FCSTD DOCUMENT  (FreeCAD 0.19R)
Label: Board Outline
License: All rights reserved
LicenseURL: http://en.wikipedia.org/wiki/All_rights_reserved
objects: Sketcher::SketchObject×1, PartDesign::Body×1
note: 2 computed .brp shape members not serialized (recipe doc carries the construction recipe); baked Part::Feature solids carry a one-line shape summary decoded from their .brp

FEATURE [Sketcher::SketchObject] Sketch
  FullyConstrained = true
  MapMode = 5
  Support = -> [XY_Plane]
  sketch-geometry (24):
    g0: LineSegment StartX=0 StartY=0 StartZ=0 EndX=29.5 EndY=0 EndZ=0
    g1: LineSegment StartX=29.5 StartY=0 StartZ=0 EndX=29.5 EndY=22.75 EndZ=0
    g2: LineSegment StartX=29.5 StartY=38.5 StartZ=0 EndX=14.57 EndY=38.5 EndZ=0
    g3: LineSegment StartX=0 StartY=38.5 StartZ=0 EndX=0 EndY=15.75 EndZ=0
    g4: LineSegment StartX=29.5 StartY=22.75 StartZ=0 EndX=37.075 EndY=22.75 EndZ=0
    g5: LineSegment StartX=37.075 StartY=22.75 StartZ=0 EndX=37.075 EndY=30.75 EndZ=0
    g6: LineSegment StartX=37.075 StartY=30.75 StartZ=0 EndX=29.5 EndY=30.75 EndZ=0
    g7: LineSegment StartX=0 StartY=15.75 StartZ=0 EndX=-7.575 EndY=15.75 EndZ=0
    g8: LineSegment StartX=-7.575 StartY=15.75 StartZ=0 EndX=-7.575 EndY=7.75 EndZ=0
    g9: LineSegment StartX=-7.575 StartY=7.75 StartZ=0 EndX=0 EndY=7.75 EndZ=0
    g10: LineSegment StartX=29.5 StartY=30.75 StartZ=0 EndX=29.5 EndY=38.5 EndZ=0
    g11: LineSegment StartX=0 StartY=7.75 StartZ=0 EndX=0 EndY=0 EndZ=0
    g12: Circle CenterX=33.7643 CenterY=26.75 CenterZ=0 NormalX=0 NormalY=0 NormalZ=1 AngleXU=0 Radius=1.95
    g13: Circle CenterX=-4.2643 CenterY=11.75 CenterZ=0 NormalX=0 NormalY=0 NormalZ=1 AngleXU=0 Radius=1.95
    g14: LineSegment StartX=33.7643 StartY=26.75 StartZ=0 EndX=33.7643 EndY=30.75 EndZ=0
    g15: LineSegment StartX=33.7643 StartY=26.75 StartZ=0 EndX=33.7643 EndY=22.75 EndZ=0
    g16: LineSegment StartX=-4.2643 StartY=11.75 StartZ=0 EndX=-4.2643 EndY=15.75 EndZ=0
    g17: LineSegment StartX=-4.2643 StartY=11.75 StartZ=0 EndX=-4.2643 EndY=7.75 EndZ=0
    g18: LineSegment StartX=-4.2643 StartY=11.75 StartZ=0 EndX=-7.575 EndY=11.75 EndZ=0
    g19: LineSegment StartX=33.7643 StartY=26.75 StartZ=0 EndX=37.075 EndY=26.75 EndZ=0
    g20: LineSegment StartX=3.78 StartY=38.5 StartZ=0 EndX=3.78 EndY=33.5 EndZ=0
    g21: LineSegment StartX=3.78 StartY=33.5 StartZ=0 EndX=14.57 EndY=33.5 EndZ=0
    g22: LineSegment StartX=14.57 StartY=33.5 StartZ=0 EndX=14.57 EndY=38.5 EndZ=0
    g23: LineSegment StartX=3.78 StartY=38.5 StartZ=0 EndX=0 EndY=38.5 EndZ=0
  constraints (68):
    c: Coincident(g0,g1)
    c: Coincident(g10,g2)
    c: Coincident(g23,g3)
    c: Coincident(g11,g0)
    c: Horizontal(g0)
    c: Horizontal(g2)
    c: Vertical(g1)
    c: Vertical(g3)
    c: Coincident(g0,g-1)
    c: DistanceX(g0,g0) = 29.5
    c: DistanceY(g1,g10) = 38.5
    c: Horizontal(g4)
    c: Coincident(g5,g4)
    c: Vertical(g5)
    c: Horizontal(g6)
    c: Horizontal(g7)
    c: Coincident(g7,g8)
    c: Vertical(g8)
    c: Coincident(g8,g9)
    c: Horizontal(g9)
    c: Coincident(g1,g4)
    c: Coincident(g10,g6)
    c: Tangent(g1,g10)
    c: Coincident(g3,g7)
    c: Coincident(g11,g9)
    c: Tangent(g3,g11)
    c: DistanceY(g5,g5) = 8
    c: DistanceY(g8,g8) = 8
    c: DistanceY(g11,g11) = 7.75
    c: DistanceY(g10,g10) = 7.75
    c: Coincident(g5,g6)
    c: Equal(g13,g12)
    c: Radius(g12) = 1.95
    c: Coincident(g14,g12)
    c: PointOnObject(g14,g6)
    c: Vertical(g14)
    c: Coincident(g15,g12)
    c: PointOnObject(g15,g4)
    c: Vertical(g15)
    c: Coincident(g16,g13)
    c: PointOnObject(g16,g7)
    c: Vertical(g16)
    c: Coincident(g17,g13)
    c: PointOnObject(g17,g9)
    c: Vertical(g17)
    c: Equal(g17,g16)
    c: Equal(g14,g15)
    c: DistanceX(g7,g5) = 44.65
    c: Equal(g7,g6)
    c: Distance(g13,g12) = 40.88
    c: Coincident(g18,g13)
    c: PointOnObject(g18,g8)
    c: Horizontal(g18)
    c: Coincident(g19,g12)
    c: PointOnObject(g19,g5)
    c: Horizontal(g19)
    c: Equal(g19,g18)
    c: Vertical(g20)
    c: Coincident(g21,g20)
    c: Horizontal(g21)
    c: Coincident(g22,g21)
    c: Vertical(g22)
    c: Coincident(g2,g22)
    c: Coincident(g23,g20)
    c: Tangent(g2,g23)
    c: DistanceY(g22,g22) = 5
    c: DistanceX(g23,g23) = 3.78
    c: DistanceX(g2,g2) = 14.93
FEATURE [PartDesign::Body] Body
  Group = -> [Sketch]
  Origin = -> Origin
